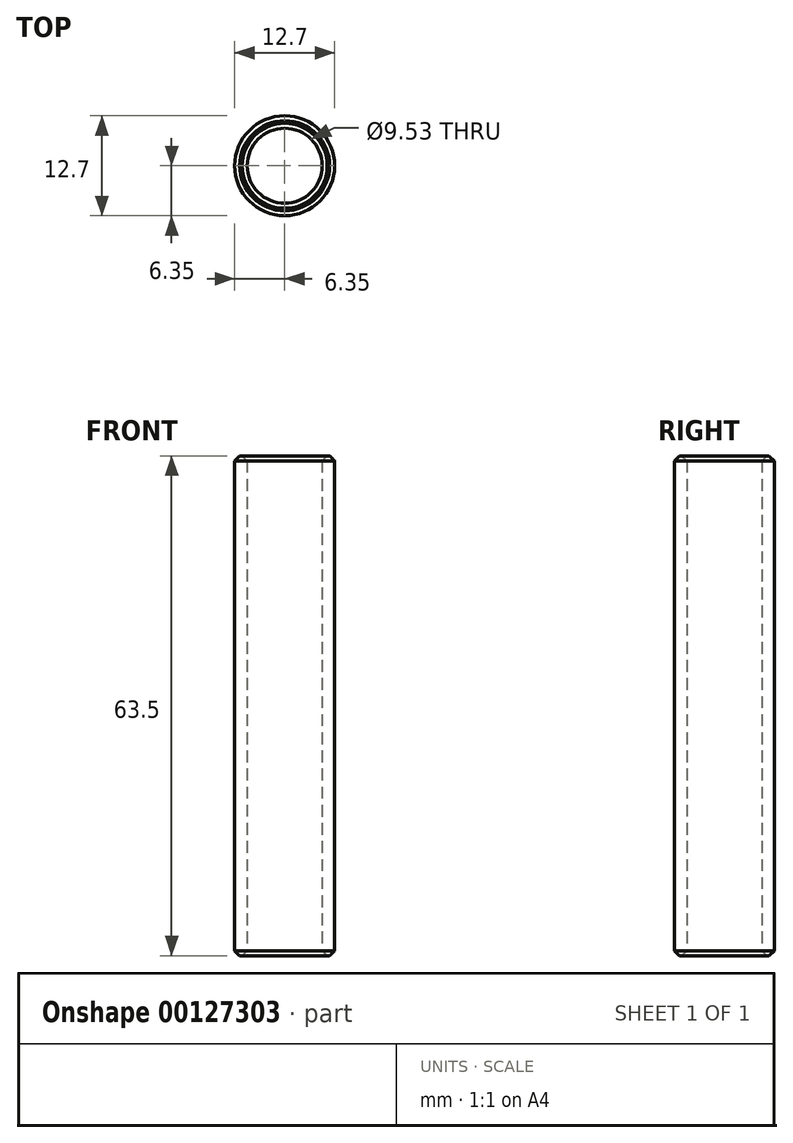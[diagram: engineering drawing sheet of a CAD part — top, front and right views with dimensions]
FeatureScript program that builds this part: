
annotation { "Feature Type Name" : "Feature", "Feature Type Description" : "" }
export const myFeature = defineFeature(function(context is Context, id is Id, definition is map)
    precondition{}
    {
        {
            var Q0;
            Q0=qCreatedBy(makeId("Top.planeOp"),FACE);
            var sketch = newSketch(context, id + "F0", { "sketchPlane" : qUnion([Q0])});
            skCircle(sketch, "E0", {"center": v(0, 0) * mm, "radius": 6.35 * mm});
            skCircle(sketch, "E1", {"center": v(0, 0) * mm, "radius": 4.76 * mm});
            skSolve(sketch);
        }
        {
            var Q0;
            Q0 = qSketchRegion(id + "F0", true);
            extrude(context, id + "F1", {"entities" : qUnion([Q0]), "depth" : 63.5 * mm});
        }
        {
            var Q0;
            Q0=makeQuery(id+"F1.opExtrude","SWEPT_FACE",FACE,{"disambiguationData":[OSD([sQuery(id+"F0.wireOp",EDGE,"E0")])]});
            var Q1;
            Q1=makeQuery(id+"F1.opExtrude","SWEPT_FACE",FACE,{"disambiguationData":[OSD([sQuery(id+"F0.wireOp",EDGE,"E1")])]});
            chamfer(context, id + "F2", {"entities" : qUnion([Q0, Q1]), "width" : 0.64 * mm, "tangentPropagation" : true});
        }
    });
